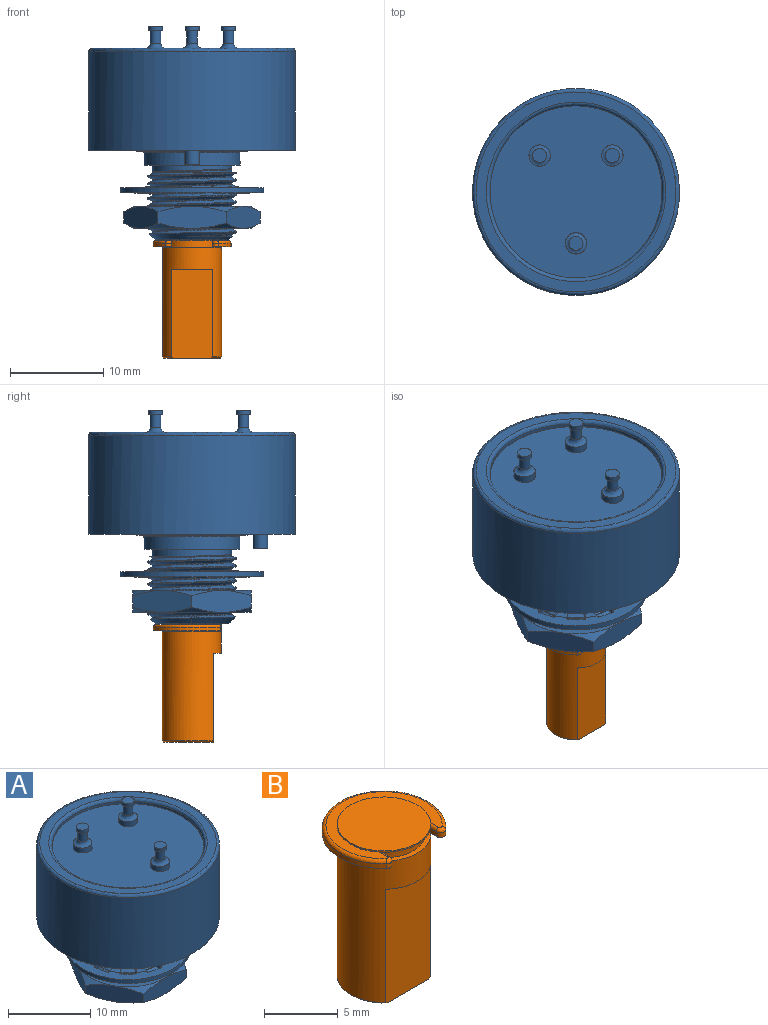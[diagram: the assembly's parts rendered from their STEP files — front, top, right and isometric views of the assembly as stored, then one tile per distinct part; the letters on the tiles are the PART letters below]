
ASSEMBLY  parts=2 mates=1
PART A: 252 faces, bbox 22.8x22.8x23.6 mm
  f0: cylinder r=3.17mm len=10.01mm, axis (0,0,1), area 199.4mm2, adj f1,f251
  f1: plane 6.36x6.36mm, normal (0,0,-1), area 0.2mm2, adj f0,f2
  f2: cylinder r=3.18mm len=9.83mm, axis (0,0,1), area 196.5mm2, adj f1,f3
  f3: cone r=3.36mm half-angle=45deg, axis (0,0,-1), area 5.2mm2, adj f2,f37
  f4: bspline ~1.93x0.78mm, area 0.9mm2, adj f5,f98,f186,f216,f217,f229
  f5: bspline ~2.02x1.92mm, area 1.6mm2, adj f4,f157,f159,f202,f216,f227
  f6: bspline ~1.9x0.71mm, area 0.9mm2, adj f7,f101,f182,f214,f215,f227,f229
  f7: bspline ~1.9x1.34mm, area 1.7mm2, adj f6,f159,f211,f215,f227
  f8: bspline ~1.93x0.78mm, area 0.9mm2, adj f9,f94,f187,f202,f219,f227
  f9: bspline ~2.02x1.92mm, area 1.7mm2, adj f8,f156,f219,f220,f229
  f10: bspline ~1.9x0.71mm, area 0.9mm2, adj f11,f91,f181,f189,f201,f221,f227
  f11: bspline ~1.9x1.34mm, area 1.7mm2, adj f10,f156,f221,f222,f229
  f12: plane 1.5x1.5mm, normal (0,0,1), area 1.8mm2, adj f15
  f13: plane 1.5x1.5mm, normal (0,0,1), area 1.8mm2, adj f16
  f14: plane 1.5x1.5mm, normal (0,0,1), area 1.8mm2, adj f17
  f15: cylinder r=0.75mm len=1.5mm, axis (0,0,1), area 2.4mm2, adj f12,f18
  f16: cylinder r=0.75mm len=1.5mm, axis (0,0,1), area 2.4mm2, adj f13,f19
  f17: cylinder r=0.75mm len=1.5mm, axis (0,0,1), area 2.4mm2, adj f14,f20
  f18: plane 1.5x1.5mm, normal (0,0,-1), area 0.7mm2, adj f15,f21
  f19: plane 1.5x1.5mm, normal (0,0,-1), area 0.7mm2, adj f16,f22
  f20: plane 1.5x1.5mm, normal (0,0,-1), area 0.7mm2, adj f17,f23
  f21: cylinder r=0.57mm len=1.35mm, axis (0,0,1), area 4.8mm2, adj f18,f24
  f22: cylinder r=0.57mm len=1.35mm, axis (0,0,1), area 4.8mm2, adj f19,f25
  f23: cylinder r=0.57mm len=1.35mm, axis (0,0,1), area 4.8mm2, adj f20,f26
  f24: revolved ~2.26x2.26mm, area 4.3mm2, adj f21,f27
  f25: revolved ~2.26x2.26mm, area 4.3mm2, adj f22,f28
  f26: revolved ~2.26x2.26mm, area 4.3mm2, adj f23,f29
  f27: plane 2.29x2.29mm, normal (0,0,1), area 0.1mm2, adj f24,f42
  f28: plane 2.29x2.29mm, normal (0,0,1), area 0.1mm2, adj f25,f43
  f29: plane 2.29x2.29mm, normal (0,0,1), area 0.1mm2, adj f26,f44
  f30: bspline ~1.88x0.71mm, area 0.9mm2, adj f53,f54,f128,f146,f181,f210,f227
  f31: cone r=7.34mm half-angle=60deg, axis (0,0,1), area 4mm2, adj f50,f51,f59
  f32: cone r=7.34mm half-angle=60deg, axis (0,0,1), area 4mm2, adj f46,f51,f59
  f33: cone r=7.34mm half-angle=60deg, axis (0,0,1), area 4mm2, adj f46,f47,f59
  f34: cone r=7.34mm half-angle=60deg, axis (0,0,1), area 4mm2, adj f47,f48,f59
  f35: cone r=7.34mm half-angle=60deg, axis (0,0,1), area 4mm2, adj f48,f49,f59
  f36: cone r=7.34mm half-angle=60deg, axis (0,0,1), area 4mm2, adj f49,f50,f59
  f37: plane 7.9x7.9mm, normal (0,0,-1), area 13.6mm2, adj f3,f58,f61
  f38: bspline ~1.87x1.34mm, area 1.6mm2, adj f63,f82,f156,f181,f204,f205,f227
  f39: bspline ~2x1.91mm, area 1.6mm2, adj f64,f81,f156,f206,f207,f227
  f40: bspline ~2.19x1.6mm, area 1.7mm2, adj f65,f80,f156,f209,f227
  f41: bspline ~2.01x1.92mm, area 1.7mm2, adj f66,f78,f156,f199,f227
  f42: cylinder r=1.14mm len=2.29mm, axis (0,0,1), area 5.5mm2, adj f27,f67
  f43: cylinder r=1.14mm len=2.29mm, axis (0,0,1), area 5.5mm2, adj f28,f68
  f44: cylinder r=1.14mm len=2.29mm, axis (0,0,1), area 5.5mm2, adj f29,f69
  f45: bspline ~1.9x0.77mm, area 0.9mm2, adj f70,f71,f109,f181,f204,f227
  f46: plane 7.92x2.95mm, normal (0,1,0), area 14.5mm2, adj f32,f33,f47,f51,f72,f73
  f47: plane 6.94x4.26mm, normal (-0.87,0.5,0), area 14.5mm2, adj f33,f34,f46,f48,f73,f74
  f48: plane 6.94x4.26mm, normal (-0.87,-0.5,0), area 14.5mm2, adj f34,f35,f47,f49,f74,f75
  f49: plane 7.92x2.95mm, normal (0,-1,0), area 14.5mm2, adj f35,f36,f48,f50,f75,f76
  f50: plane 6.94x4.26mm, normal (0.87,-0.5,0), area 14.5mm2, adj f31,f36,f49,f51,f76,f77
  f51: plane 6.94x4.26mm, normal (0.87,0.5,0), area 14.5mm2, adj f31,f32,f46,f50,f72,f77
  f52: bspline ~2.19x1.6mm, area 1.6mm2, adj f66,f78,f144,f159,f181,f200,f227
  f53: bspline ~1.87x1.34mm, area 1.6mm2, adj f30,f79,f145,f146,f159,f181
  f54: bspline ~1.88x1.34mm, area 1.7mm2, adj f30,f79,f156,f198,f227
  f55: bspline ~2x1.91mm, area 1.6mm2, adj f65,f80,f147,f159,f181,f210
  f56: bspline ~2.19x1.6mm, area 1.7mm2, adj f64,f81,f148,f159,f181
  f57: bspline ~1.88x1.34mm, area 1.7mm2, adj f63,f82,f149,f159,f181
  f58: cone r=4.58mm half-angle=45deg, axis (0,0,1), area 9.3mm2, adj f37,f61,f83
  f59: plane 12.71x12.71mm, normal (0,0,-1), area 59.5mm2, adj f31,f32,f33,f34,f35,f36,f62,f83
  f60: bspline ~8.62x8.61mm, area 7.7mm2, adj f61,f83,f84,f151
  f61: cone r=4.76mm half-angle=45deg, axis (0,0,1), area 11.7mm2, adj f37,f58,f60,f62,f83,f84
  f62: cylinder r=4.76mm len=9.53mm, axis (0,0,1), area 1.5mm2, adj f59,f61,f83,f84
  f63: bspline ~1.88x0.71mm, area 0.9mm2, adj f38,f57,f114,f181,f205,f206,f227
  f64: bspline ~1.53x1.43mm, area 0.9mm2, adj f39,f56,f119,f181,f207,f208,f227
  f65: bspline ~1.91x0.78mm, area 0.9mm2, adj f40,f55,f124,f209,f210,f227
  f66: bspline ~1.54x1.44mm, area 1mm2, adj f41,f52,f134,f199,f227
  f67: plane 2.29x2.29mm, normal (0,0,-1), area 2.9mm2, adj f42,f139
  f68: plane 2.29x2.29mm, normal (0,0,-1), area 2.9mm2, adj f43,f140
  f69: plane 2.29x2.29mm, normal (0,0,-1), area 2.9mm2, adj f44,f141
  f70: bspline ~2.18x1.59mm, area 1.6mm2, adj f45,f142,f156,f181,f203,f227
  f71: bspline ~2.01x1.91mm, area 1.7mm2, adj f45,f142,f150,f159,f180,f181
  f72: cone r=7.34mm half-angle=60deg, axis (0,0,-1), area 4mm2, adj f46,f51,f143
  f73: cone r=7.34mm half-angle=60deg, axis (0,0,-1), area 4mm2, adj f46,f47,f143
  f74: cone r=7.34mm half-angle=60deg, axis (0,0,-1), area 4mm2, adj f47,f48,f143
  f75: cone r=7.34mm half-angle=60deg, axis (0,0,-1), area 4mm2, adj f48,f49,f143
  f76: cone r=7.34mm half-angle=60deg, axis (0,0,-1), area 4mm2, adj f49,f50,f143
  f77: cone r=7.34mm half-angle=60deg, axis (0,0,-1), area 4mm2, adj f50,f51,f143
  f78: bspline ~1.91x0.77mm, area 0.9mm2, adj f41,f52,f133,f144,f145,f181,f227
  f79: bspline ~1.89x0.71mm, area 0.9mm2, adj f53,f54,f129,f145,f198,f227
  f80: bspline ~1.53x1.43mm, area 0.9mm2, adj f40,f55,f123,f147,f181,f208,f227
  f81: bspline ~1.92x0.78mm, area 0.9mm2, adj f39,f56,f118,f148,f181,f206
  f82: bspline ~1.89x0.71mm, area 1mm2, adj f38,f57,f113,f149,f181
  f83: bspline ~9.67x9.62mm, area 30.2mm2, adj f58,f59,f60,f61,f62,f152,f180
  f84: bspline ~9.69x9.67mm, area 34mm2, adj f59,f60,f61,f62,f152,f181
  f85: bspline ~2.2x1.6mm, area 1.7mm2, adj f154,f159,f212,f213,f227
  f86: cylinder r=7.68mm len=15.37mm, axis (0,0,1), area 27mm2, adj f156,f159
  f87: cylinder r=6.53mm len=1.27mm, axis (0,0,1), area 1mm2, adj f88,f135,f156,f159
  f88: cylinder r=0.15mm len=0.56mm, axis (0,0,-1), area 0.1mm2, adj f87,f136,f156,f159
  f89: cylinder r=6.53mm len=1.74mm, axis (0,0,1), area 1mm2, adj f90,f156,f159,f161
  f90: cylinder r=0.15mm len=0.56mm, axis (0,0,-1), area 0.1mm2, adj f89,f91,f156,f159
  f91: plane 0.56x0.08mm, normal (-1,0,0), area 0mm2, adj f10,f90,f156,f159
  f92: cylinder r=6.53mm len=1.74mm, axis (0,0,1), area 1mm2, adj f93,f156,f159,f160
  f93: cylinder r=0.15mm len=0.56mm, axis (0,0,-1), area 0.1mm2, adj f92,f94,f156,f159
  f94: plane 0.56x0.07mm, normal (-0.87,0.5,0), area 0mm2, adj f8,f93,f156,f159
  f95: cylinder r=6.53mm len=1.27mm, axis (0,0,1), area 1mm2, adj f96,f156,f158,f159
  f96: cylinder r=0.15mm len=0.56mm, axis (0,0,-1), area 0.1mm2, adj f95,f97,f156,f159
  f97: plane 0.56x0.07mm, normal (-0.5,0.87,0), area 0mm2, adj f96,f156,f157,f159
  f98: plane 0.56x0.07mm, normal (0.5,-0.87,0), area 0mm2, adj f4,f99,f156,f159
  f99: cylinder r=0.15mm len=0.56mm, axis (0,0,1), area 0.1mm2, adj f98,f100,f156,f159
  f100: cylinder r=6.53mm len=1.74mm, axis (0,0,1), area 1mm2, adj f99,f153,f156,f159
  f101: plane 0.56x0.08mm, normal (0,-1,0), area 0mm2, adj f6,f102,f156,f159
  f102: cylinder r=0.15mm len=0.56mm, axis (0,0,1), area 0.1mm2, adj f101,f103,f156,f159
  f103: cylinder r=6.53mm len=1.74mm, axis (0,0,1), area 1mm2, adj f102,f155,f156,f159
  f104: plane 0.56x0.07mm, normal (-0.5,-0.87,0), area 0mm2, adj f105,f154,f156,f159
  f105: cylinder r=0.15mm len=0.56mm, axis (0,0,1), area 0.1mm2, adj f104,f106,f156,f159
  f106: cylinder r=6.53mm len=1.27mm, axis (0,0,1), area 1mm2, adj f105,f107,f156,f159
  f107: cylinder r=0.15mm len=0.56mm, axis (0,0,-1), area 0.1mm2, adj f106,f108,f156,f159
  f108: plane 0.56x0.07mm, normal (0.87,0.5,0), area 0mm2, adj f107,f142,f156,f159
  f109: plane 0.56x0.07mm, normal (-0.87,-0.5,0), area 0mm2, adj f45,f110,f156,f159
  f110: cylinder r=0.15mm len=0.56mm, axis (0,0,1), area 0.1mm2, adj f109,f111,f156,f159
  f111: cylinder r=6.53mm len=1.74mm, axis (0,0,1), area 1mm2, adj f110,f112,f156,f159
  f112: cylinder r=0.15mm len=0.56mm, axis (0,0,-1), area 0.1mm2, adj f111,f113,f156,f159
  f113: plane 0.56x0.08mm, normal (1,0,0), area 0mm2, adj f82,f112,f156,f159
  f114: plane 0.56x0.08mm, normal (-1,0,0), area 0mm2, adj f63,f115,f156,f159
  f115: cylinder r=0.15mm len=0.56mm, axis (0,0,1), area 0.1mm2, adj f114,f116,f156,f159
  f116: cylinder r=6.53mm len=1.74mm, axis (0,0,1), area 1mm2, adj f115,f117,f156,f159
  f117: cylinder r=0.15mm len=0.56mm, axis (0,0,-1), area 0.1mm2, adj f116,f118,f156,f159
  f118: plane 0.56x0.07mm, normal (0.87,-0.5,0), area 0mm2, adj f81,f117,f156,f159
  f119: plane 0.56x0.07mm, normal (-0.87,0.5,0), area 0mm2, adj f64,f120,f156,f159
  f120: cylinder r=0.15mm len=0.56mm, axis (0,0,1), area 0.1mm2, adj f119,f121,f156,f159
  f121: cylinder r=6.53mm len=1.27mm, axis (0,0,1), area 1mm2, adj f120,f122,f156,f159
  f122: cylinder r=0.15mm len=0.56mm, axis (0,0,-1), area 0.1mm2, adj f121,f123,f156,f159
  f123: plane 0.56x0.07mm, normal (0.5,-0.87,0), area 0mm2, adj f80,f122,f156,f159
  f124: plane 0.56x0.07mm, normal (-0.5,0.87,0), area 0mm2, adj f65,f125,f156,f159
  f125: cylinder r=0.15mm len=0.56mm, axis (0,0,1), area 0.1mm2, adj f124,f126,f156,f159
  f126: cylinder r=6.53mm len=1.74mm, axis (0,0,1), area 1mm2, adj f125,f127,f156,f159
  f127: cylinder r=0.15mm len=0.56mm, axis (0,0,-1), area 0.1mm2, adj f126,f128,f156,f159
  f128: plane 0.56x0.08mm, normal (0,-1,0), area 0mm2, adj f30,f127,f156,f159
  f129: plane 0.56x0.08mm, normal (0,1,0), area 0mm2, adj f79,f130,f156,f159
  f130: cylinder r=0.15mm len=0.56mm, axis (0,0,1), area 0.1mm2, adj f129,f131,f156,f159
  f131: cylinder r=6.53mm len=1.74mm, axis (0,0,1), area 1mm2, adj f130,f132,f156,f159
  f132: cylinder r=0.15mm len=0.56mm, axis (0,0,-1), area 0.1mm2, adj f131,f133,f156,f159
  f133: plane 0.58x0.09mm, normal (-0.5,-0.87,0), area 0mm2, adj f78,f132,f156,f159
  f134: plane 0.56x0.07mm, normal (0.5,0.87,0), area 0mm2, adj f66,f135,f156,f159
  f135: cylinder r=0.15mm len=0.56mm, axis (0,0,1), area 0.1mm2, adj f87,f134,f156,f159
  f136: plane 0.56x0.07mm, normal (-0.87,-0.5,0), area 0mm2, adj f88,f156,f159,f162
  f137: cylinder r=10.16mm len=8.56mm, axis (0,0,1), area 16.9mm2, adj f178,f179,f195,f197
  f138: cylinder r=10.16mm len=20.27mm, axis (0,0,1), area 66.3mm2, adj f163,f164,f165,f166,f167,f168,f169,f170
  f139: cylinder r=0.61mm len=1.22mm, axis (0,0,1), area 0.5mm2, adj f67,f179
  f140: cylinder r=0.61mm len=1.22mm, axis (0,0,1), area 0.5mm2, adj f68,f179
  f141: cylinder r=0.61mm len=1.22mm, axis (0,0,1), area 0.5mm2, adj f69,f179
  f142: bspline ~1.54x1.44mm, area 1mm2, adj f70,f71,f108,f150,f180,f181
  f143: plane 12.71x12.71mm, normal (0,0,1), area 59.5mm2, adj f72,f73,f74,f75,f76,f77,f152,f180
  f144: cylinder r=4.45mm len=0.05mm, axis (0,0,1), area 0mm2, adj f52,f78,f181
  f145: cylinder r=4.76mm len=1.8mm, axis (0,0,1), area 0.2mm2, adj f53,f78,f79,f181,f227
  f146: cylinder r=4.45mm len=0.2mm, axis (0,0,1), area 0mm2, adj f30,f53,f181
  f147: cylinder r=4.45mm len=0.3mm, axis (0,0,1), area 0mm2, adj f55,f80,f181
  f148: cylinder r=4.45mm len=0.42mm, axis (0,0,1), area 0.1mm2, adj f56,f81,f181
  f149: cylinder r=4.45mm len=0.63mm, axis (0,0,1), area 0.1mm2, adj f57,f82,f181
  f150: cylinder r=4.45mm len=0.67mm, axis (0,0,1), area 0.1mm2, adj f71,f142,f180,f181
  f151: bspline ~8.64x8.63mm, area 8.4mm2, adj f60,f180,f181,f218
  f152: cylinder r=4.57mm len=9.14mm, axis (0,0,1), area 40.6mm2, adj f59,f83,f84,f143,f180,f181
  f153: cylinder r=0.15mm len=0.56mm, axis (0,0,-1), area 0.1mm2, adj f100,f156,f159,f183
  f154: bspline ~1.55x1.45mm, area 0.9mm2, adj f85,f104,f184,f203,f213,f227,f229
  f155: cylinder r=0.15mm len=0.56mm, axis (0,0,-1), area 0.1mm2, adj f103,f156,f159,f185
  f156: plane 15.37x15.37mm, normal (0,0,1), area 55.8mm2, adj f9,f11,f38,f39,f40,f41,f54,f70
  f157: bspline ~1.55x1.45mm, area 0.9mm2, adj f5,f97,f186,f202,f216,f227
  f158: cylinder r=0.15mm len=0.56mm, axis (0,0,1), area 0.1mm2, adj f95,f156,f159,f188
  f159: plane 15.37x15.37mm, normal (0,0,-1), area 55.8mm2, adj f5,f7,f52,f53,f55,f56,f57,f71
  f160: cylinder r=0.15mm len=0.56mm, axis (0,0,1), area 0.1mm2, adj f92,f156,f159,f190
  f161: cylinder r=0.15mm len=0.56mm, axis (0,0,1), area 0.1mm2, adj f89,f156,f159,f192
  f162: bspline ~1.52x1.42mm, area 0.9mm2, adj f136,f181,f191,f193,f200,f227
  f163: plane 8.31x6.74mm, normal (0,0,1), area 0.6mm2, adj f138,f164,f194,f195
  f164: plane 0.76x0.05mm, normal (1,0,0), area 0mm2, adj f138,f163,f165,f194
  f165: plane 0.88x0.12mm, normal (0,0,1), area 0mm2, adj f138,f164,f166,f194
  f166: plane 2.04x0.43mm, normal (-0.85,0.49,0.18), area 0.1mm2, adj f138,f165,f167,f194
  f167: plane 2.04x0.43mm, normal (0.85,0.49,0.18), area 0.1mm2, adj f138,f166,f168,f194
  f168: plane 0.88x0.12mm, normal (0,0,1), area 0mm2, adj f138,f167,f169,f194
  f169: plane 0.76x0.05mm, normal (-1,0,0), area 0mm2, adj f138,f168,f170,f194
  f170: plane 8.86x8.86mm, normal (0,0,1), area 0.7mm2, adj f138,f169,f171,f194
  f171: plane 0.76x0.05mm, normal (0,1,0), area 0mm2, adj f138,f170,f172,f194
  f172: plane 0.88x0.12mm, normal (0,0,1), area 0mm2, adj f138,f171,f173,f194
  f173: plane 2.04x0.43mm, normal (-0.49,-0.85,0.18), area 0.1mm2, adj f138,f172,f174,f194
  f174: plane 2.04x0.43mm, normal (-0.49,0.85,0.18), area 0.1mm2, adj f138,f173,f175,f194
  f175: plane 0.88x0.12mm, normal (0,0,1), area 0mm2, adj f138,f174,f176,f194
  f176: plane 0.76x0.05mm, normal (0,-1,0), area 0mm2, adj f138,f175,f177,f194
  f177: plane 9.12x8.84mm, normal (0,0,1), area 0.7mm2, adj f138,f176,f194,f197
  f178: plane 8.56x6.71mm, normal (0,0,1), area 0.6mm2, adj f137,f195,f196,f197
  f179: plane 20.27x19.74mm, normal (0,0,1), area 318.1mm2, adj f137,f138,f139,f140,f141,f195,f197
  f180: bspline ~9.71x9.7mm, area 43.4mm2, adj f71,f83,f142,f143,f150,f151,f152,f202
  f181: bspline ~9.71x9.7mm, area 46.8mm2, adj f10,f30,f38,f45,f52,f53,f55,f56
  f182: bspline ~1.9x1.34mm, area 1.6mm2, adj f6,f156,f211,f215,f217,f227,f229
  f183: plane 0.56x0.08mm, normal (0,1,0), area 0mm2, adj f153,f156,f159,f211
  f184: bspline ~2.02x1.92mm, area 1.6mm2, adj f154,f156,f212,f213,f214,f227,f229
  f185: plane 0.56x0.07mm, normal (0.5,0.87,0), area 0mm2, adj f155,f156,f159,f212
  f186: bspline ~2.2x1.6mm, area 1.6mm2, adj f4,f156,f157,f216,f217,f229
  f187: bspline ~2.2x1.6mm, area 1.6mm2, adj f8,f159,f202,f219,f220,f227
  f188: plane 0.56x0.07mm, normal (0.87,-0.5,0), area 0mm2, adj f156,f158,f159,f220
  f189: bspline ~1.9x1.34mm, area 1.6mm2, adj f10,f159,f181,f202,f221,f222,f227
  f190: plane 0.56x0.08mm, normal (1,0,0), area 0mm2, adj f156,f159,f160,f222
  f191: bspline ~2x1.91mm, area 1.6mm2, adj f159,f162,f181,f201,f224,f227
  f192: plane 0.56x0.07mm, normal (0.87,0.5,0), area 0mm2, adj f156,f159,f161,f224
  f193: bspline ~2.2x1.6mm, area 1.7mm2, adj f156,f162,f223,f224,f227,f229
  f194: cylinder r=10.21mm len=20.32mm, axis (0,0,1), area 70mm2, adj f163,f164,f165,f166,f167,f168,f169,f170
  f195: plane 7.09x1.57mm, normal (1,0,0), area 1.2mm2, adj f137,f138,f163,f178,f179,f194,f196,f225
  f196: cylinder r=10.21mm len=8.14mm, axis (0,0,1), area 17.3mm2, adj f178,f195,f197,f225
  f197: plane 2.87x1.57mm, normal (0,-1,0), area 1.5mm2, adj f137,f138,f177,f178,f179,f194,f196,f225
  f198: cylinder r=4.45mm len=0.56mm, axis (0,0,1), area 0.1mm2, adj f54,f79,f227
  f199: cylinder r=4.45mm len=0.61mm, axis (0,0,1), area 0.1mm2, adj f41,f66,f227
  f200: cylinder r=4.76mm len=1.45mm, axis (0,0,1), area 0.2mm2, adj f52,f162,f181,f227
  f201: cylinder r=4.76mm len=2.11mm, axis (0,0,1), area 0.2mm2, adj f10,f181,f191,f227
  f202: cylinder r=4.76mm len=9.53mm, axis (0,0,1), area 5.4mm2, adj f5,f8,f143,f157,f180,f181,f187,f189
  f203: cylinder r=4.76mm len=1.51mm, axis (0,0,1), area 0.2mm2, adj f70,f154,f181,f227,f229
  f204: cylinder r=4.76mm len=1.88mm, axis (0,0,1), area 0.2mm2, adj f38,f45,f181,f227
  f205: cylinder r=4.45mm len=0.13mm, axis (0,0,1), area 0mm2, adj f38,f63,f227
  f206: cylinder r=4.76mm len=1.72mm, axis (0,0,1), area 0.2mm2, adj f39,f63,f81,f181,f227
  f207: cylinder r=4.45mm len=0.24mm, axis (0,0,1), area 0mm2, adj f39,f64,f227
  f208: cylinder r=4.76mm len=1.2mm, axis (0,0,1), area 0.2mm2, adj f64,f80,f181,f227
  f209: cylinder r=4.45mm len=0.37mm, axis (0,0,1), area 0mm2, adj f40,f65,f227
  f210: cylinder r=4.76mm len=1.64mm, axis (0,0,1), area 0.2mm2, adj f30,f55,f65,f181,f227
  f211: bspline ~1.9x0.71mm, area 0.9mm2, adj f7,f182,f183,f215,f227
  f212: bspline ~1.93x0.78mm, area 1mm2, adj f85,f184,f185,f213,f227
  f213: cylinder r=4.45mm len=0.77mm, axis (0,0,1), area 0.2mm2, adj f85,f154,f184,f212,f227,f229
  f214: cylinder r=4.76mm len=2.18mm, axis (0,0,1), area 0.2mm2, adj f6,f184,f227,f229
  f215: cylinder r=4.45mm len=0.89mm, axis (0,0,1), area 0.2mm2, adj f6,f7,f182,f211,f227,f229
  f216: cylinder r=4.45mm len=0.77mm, axis (0,0,1), area 0.2mm2, adj f4,f5,f157,f186,f227,f229
  f217: cylinder r=4.76mm len=9.53mm, axis (0,0,1), area 6mm2, adj f4,f182,f186,f227,f228,f229
  f218: bspline ~8.64x8.63mm, area 8.4mm2, adj f151,f226,f227,f229
  f219: cylinder r=4.45mm len=0.77mm, axis (0,0,1), area 0.2mm2, adj f8,f9,f187,f220,f227,f229
  f220: bspline ~1.55x1.45mm, area 0.9mm2, adj f9,f187,f188,f219,f229
  f221: cylinder r=4.45mm len=0.89mm, axis (0,0,1), area 0.2mm2, adj f10,f11,f189,f222,f227,f229
  f222: bspline ~1.9x0.71mm, area 1mm2, adj f11,f189,f190,f221,f229
  f223: cylinder r=4.45mm len=0.74mm, axis (0,0,1), area 0.2mm2, adj f193,f224,f227,f229
  f224: bspline ~1.93x0.78mm, area 1mm2, adj f191,f192,f193,f223,f227,f229
  f225: plane 20.32x19.79mm, normal (0,0,-1), area 55.8mm2, adj f194,f195,f196,f197,f230
  f226: plane 0.11x0.01mm, normal (0.41,-0.91,0), area 0mm2, adj f218,f227,f229,f231
  f227: bspline ~9.71x9.7mm, area 46.6mm2, adj f5,f6,f7,f8,f10,f30,f38,f39
  f228: plane 9.03x8.7mm, normal (0,0,1), area 7mm2, adj f217,f227,f229,f231,f232
  f229: bspline ~9.71x9.7mm, area 39.5mm2, adj f4,f6,f9,f11,f154,f181,f182,f184
  f230: cylinder r=9.25mm len=18.49mm, axis (0,0,-1), area 1.5mm2, adj f225,f233
  f231: cylinder r=4.25mm len=8.51mm, axis (0,0,1), area 19.8mm2, adj f226,f227,f228,f229,f232,f234
  f232: cylinder r=4.25mm len=3.81mm, axis (0,0,1), area 0.3mm2, adj f227,f228,f231
  f233: plane 18.49x18.49mm, normal (0,0,-1), area 256mm2, adj f230,f235,f236,f237
  f234: plane 10.31x10.31mm, normal (0,0,-1), area 26.7mm2, adj f231,f238
  f235: cylinder r=1.16mm len=2.31mm, axis (0,0,-1), area 0.4mm2, adj f233,f239
  f236: cylinder r=1.16mm len=2.31mm, axis (0,0,-1), area 0.4mm2, adj f233,f239
  f237: cylinder r=1.16mm len=2.31mm, axis (0,0,-1), area 0.4mm2, adj f233,f239
  f238: cylinder r=5.16mm len=10.31mm, axis (0,0,1), area 44.4mm2, adj f234,f240
  f239: plane 18.49x18.49mm, normal (0,0,1), area 256mm2, adj f235,f236,f237,f241
  f240: revolved ~10.57x10.57mm, area 6.5mm2, adj f238,f242
  f241: cylinder r=9.25mm len=18.49mm, axis (0,0,-1), area 20.7mm2, adj f239,f243
  f242: plane 11.94x11.94mm, normal (0,0,-1), area 24.1mm2, adj f240,f244
  f243: revolved ~19.25x19.25mm, area 35.3mm2, adj f241,f245
  f244: cylinder r=5.97mm len=11.94mm, axis (0,0,1), area 3.8mm2, adj f242,f246
  f245: plane 21.46x21.46mm, normal (0,0,1), area 70.8mm2, adj f243,f247
  f246: plane 22.23x22.23mm, normal (0,0,-1), area 274mm2, adj f244,f248,f249
  f247: revolved ~22.23x22.23mm, area 41.3mm2, adj f245,f248
  f248: cylinder r=11.11mm len=22.23mm, axis (0,0,1), area 737.8mm2, adj f246,f247
  f249: cylinder r=0.79mm len=1.59mm, axis (0,0,1), area 7.9mm2, adj f246,f250
  f250: plane 1.59x1.59mm, normal (0,0,-1), area 2mm2, adj f249
  f251: plane 6.34x6.34mm, normal (0,0,-1), area 31.6mm2, adj f0
PART B: 29 faces, bbox 8.4x7.4x12.7 mm
  f0: cylinder r=3.17mm len=6.34mm, axis (0,0,1), area 2mm2, adj f5,f7,f15,f16,f28
  f1: cylinder r=3.16mm len=6.31mm, axis (0,0,1), area 7.1mm2, adj f4,f5,f7,f11,f12,f16
  f2: plane 6.34x6.34mm, normal (0,0,1), area 7.1mm2, adj f3,f23
  f3: cylinder r=3.17mm len=11.73mm, axis (0,0,1), area 189mm2, adj f2,f25,f26,f27
  f4: plane 8.39x7.37mm, normal (0,0,-1), area 21.6mm2, adj f1,f6,f8,f9,f10,f11,f12,f20
  f5: plane 3.92x3.16mm, normal (0,0,-1), area 1mm2, adj f0,f1,f6,f12,f23
  f6: plane 0.64x0.36mm, normal (0,1,0), area 0.2mm2, adj f4,f5,f12,f23
  f7: plane 3.92x3.16mm, normal (0,0,-1), area 1mm2, adj f0,f1,f8,f11,f23
  f8: plane 0.64x0.36mm, normal (0,1,0), area 0.2mm2, adj f4,f7,f11,f23
  f9: plane 1.08x0.38mm, normal (-1,0,0), area 0.4mm2, adj f4,f13,f21,f23
  f10: plane 1.08x0.38mm, normal (1,0,0), area 0.4mm2, adj f4,f14,f20,f23
  f11: cylinder r=0.18mm len=0.64mm, axis (0,0,1), area 0.2mm2, adj f1,f4,f7,f8,f16
  f12: cylinder r=0.18mm len=0.64mm, axis (0,0,1), area 0.2mm2, adj f1,f4,f5,f6,f16
  f13: cylinder r=0.25mm len=1.47mm, axis (0,-1,0), area 0.5mm2, adj f9,f15,f16,f17,f23
  f14: cylinder r=0.25mm len=1.47mm, axis (0,1,0), area 0.5mm2, adj f10,f15,f16,f19,f23
  f15: plane 4.92x1.85mm, normal (0,0,-1), area 2.2mm2, adj f0,f13,f14,f23
  f16: plane 7.91x6.86mm, normal (0,0,1), area 12.8mm2, adj f0,f1,f11,f12,f13,f14,f17,f18
  f17: torus R=0.13mm, axis (0,0,1), area 0.3mm2, adj f13,f16,f18,f21
  f18: revolved ~8.36x7.27mm, area 7.8mm2, adj f16,f17,f19,f22
  f19: torus R=0.13mm, axis (0,0,1), area 0.3mm2, adj f14,f16,f18,f20
  f20: cylinder r=0.38mm len=0.64mm, axis (0,0,1), area 0.3mm2, adj f4,f10,f19,f22
  f21: cylinder r=0.38mm len=0.64mm, axis (0,0,1), area 0.3mm2, adj f4,f9,f17,f22
  f22: cylinder r=4.19mm len=8.38mm, axis (0,0,1), area 7.6mm2, adj f4,f18,f20,f21
  f23: cylinder r=2.79mm len=5.59mm, axis (0,0,1), area 12.2mm2, adj f2,f4,f5,f6,f7,f8,f9,f10
  f24: plane 6.09x5.36mm, normal (0,0,-1), area 27.1mm2, adj f25,f27
  f25: plane 9.53x4.34mm, normal (0,-1,0), area 41.3mm2, adj f3,f24,f26,f27
  f26: plane 4.33x0.86mm, normal (0,0,-1), area 2.5mm2, adj f3,f25
  f27: cone r=3.17mm half-angle=45deg, axis (0,0,1), area 2.7mm2, adj f3,f24,f25
  f28: plane 6.34x6.34mm, normal (0,0,1), area 31.6mm2, adj f0
PLACE A at identity
PLACE B at identity
MATE revolute B.f0 <-> A.f0  axis (0,0,1) through (0,0,-9.63)mm
